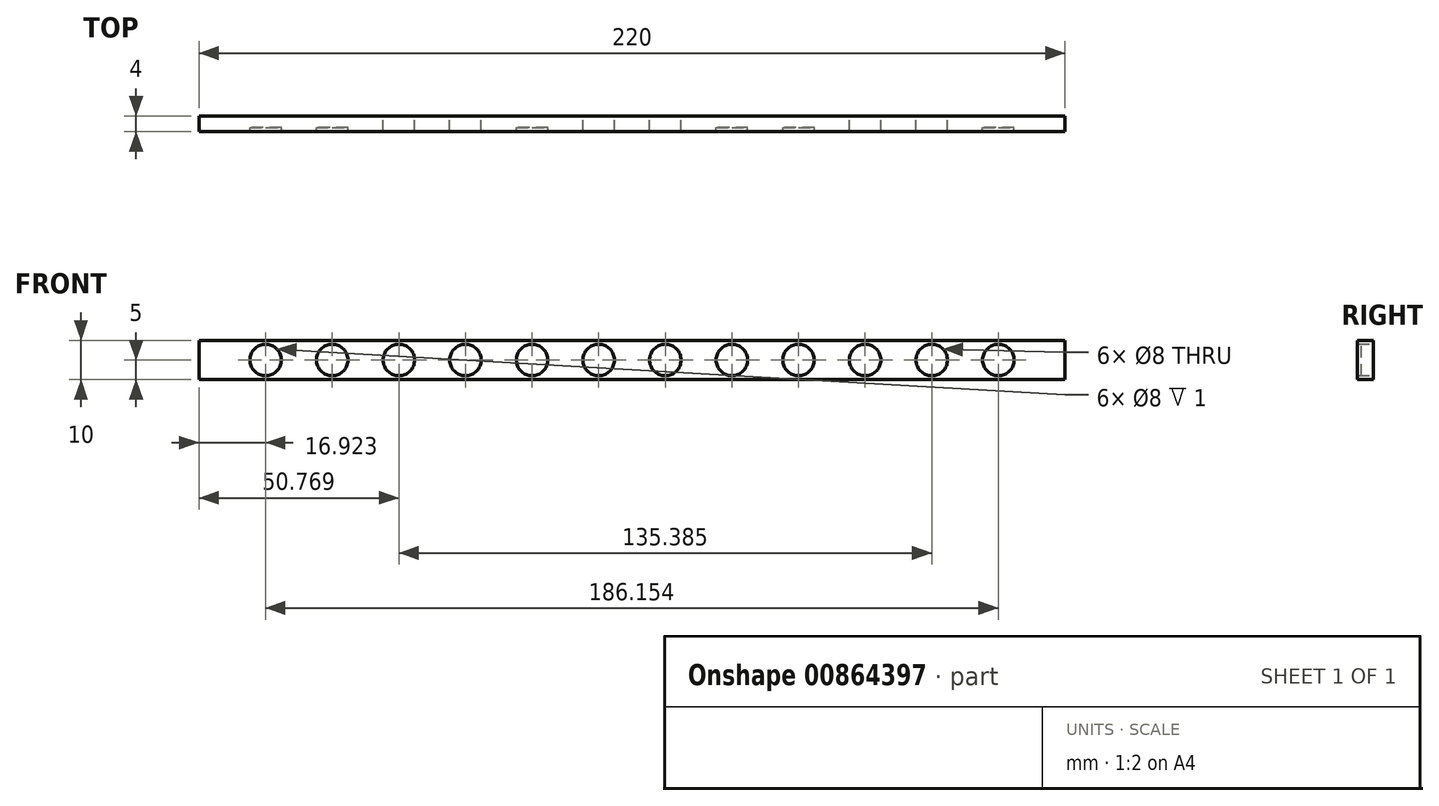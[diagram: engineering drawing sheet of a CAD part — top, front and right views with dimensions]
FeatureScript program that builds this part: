
annotation { "Feature Type Name" : "Feature", "Feature Type Description" : "" }
export const myFeature = defineFeature(function(context is Context, id is Id, definition is map)
    precondition{}
    {
        {
            var Q0;
            Q0=qCreatedBy(makeId("Front.planeOp"),FACE);
            var sketch = newSketch(context, id + "F0", { "sketchPlane" : qUnion([Q0])});
            skLineSegment(sketch, "E0", {"start": v(0, 0) * mm, "end": v(0, 10) * mm});
            skLineSegment(sketch, "E1", {"start": v(0, 10) * mm, "end": v(220, 10) * mm});
            skLineSegment(sketch, "E2", {"start": v(220, 10) * mm, "end": v(220, 0) * mm});
            skLineSegment(sketch, "E3", {"start": v(220, 0) * mm, "end": v(0, 0) * mm});
            skCircle(sketch, "E4", {"center": v(16.92, 5) * mm, "radius": 4 * mm});
            skCircle(sketch, "E5.MirrorC", {"center": v(50.77, 5) * mm, "radius": 4 * mm});
            skCircle(sketch, "E6.MirrorC", {"center": v(84.62, 5) * mm, "radius": 4 * mm});
            skCircle(sketch, "E7", {"center": v(33.85, 5) * mm, "radius": 4 * mm});
            skCircle(sketch, "E8.MirrorC", {"center": v(67.7, 5) * mm, "radius": 4 * mm});
            skCircle(sketch, "E9.MirrorC", {"center": v(118.46, 5) * mm, "radius": 4 * mm});
            skCircle(sketch, "E10.MirrorC", {"center": v(135.38, 5) * mm, "radius": 4 * mm});
            skCircle(sketch, "E11.MirrorC", {"center": v(169.23, 5) * mm, "radius": 4 * mm});
            skCircle(sketch, "E12.MirrorC", {"center": v(152.3, 5) * mm, "radius": 4 * mm});
            skCircle(sketch, "E13.MirrorC", {"center": v(186.15, 5) * mm, "radius": 4 * mm});
            skCircle(sketch, "E14.MirrorC", {"center": v(101.54, 5) * mm, "radius": 4 * mm});
            skCircle(sketch, "E15.MirrorC", {"center": v(203.08, 5) * mm, "radius": 4 * mm});
            skSolve(sketch);
        }
        {
            var Q0;
            Q0=makeQuery(id+"F0.imprint","IMPRINT",FACE,{"disambiguationData":[TD([[makeQuery(id+"F0.imprint","IMPRINT",EDGE,{"derivedFrom":sQuery(id+"F0.wireOp",EDGE,"E1")}),-1.0]])]});
            extrude(context, id + "F1", {"entities" : qUnion([Q0]), "depth" : 1 * mm, "offsetDistance" : 25 * mm});
        }
        {
            var Q0;
            Q0=makeQuery(id+"F0.imprint","IMPRINT",FACE,{"disambiguationData":[TD([[makeQuery(id+"F0.imprint","IMPRINT",EDGE,{"derivedFrom":sQuery(id+"F0.wireOp",EDGE,"E4")}),1.0]])]});
            var Q1;
            Q1=makeQuery(id+"F0.imprint","IMPRINT",FACE,{"disambiguationData":[TD([[makeQuery(id+"F0.imprint","IMPRINT",EDGE,{"derivedFrom":sQuery(id+"F0.wireOp",EDGE,"E7")}),1.0]])]});
            var Q2;
            Q2=makeQuery(id+"F0.imprint","IMPRINT",FACE,{"disambiguationData":[TD([[makeQuery(id+"F0.imprint","IMPRINT",EDGE,{"derivedFrom":sQuery(id+"F0.wireOp",EDGE,"E5.MirrorC")}),-1.0]])]});
            var Q3;
            Q3=makeQuery(id+"F0.imprint","IMPRINT",FACE,{"disambiguationData":[TD([[makeQuery(id+"F0.imprint","IMPRINT",EDGE,{"derivedFrom":sQuery(id+"F0.wireOp",EDGE,"E8.MirrorC")}),-1.0]])]});
            var Q4;
            Q4=makeQuery(id+"F0.imprint","IMPRINT",FACE,{"disambiguationData":[TD([[makeQuery(id+"F0.imprint","IMPRINT",EDGE,{"derivedFrom":sQuery(id+"F0.wireOp",EDGE,"E6.MirrorC")}),1.0]])]});
            var Q5;
            Q5=makeQuery(id+"F0.imprint","IMPRINT",FACE,{"disambiguationData":[TD([[makeQuery(id+"F0.imprint","IMPRINT",EDGE,{"derivedFrom":sQuery(id+"F0.wireOp",EDGE,"E14.MirrorC")}),-1.0]])]});
            var Q6;
            Q6=makeQuery(id+"F0.imprint","IMPRINT",FACE,{"disambiguationData":[TD([[makeQuery(id+"F0.imprint","IMPRINT",EDGE,{"derivedFrom":sQuery(id+"F0.wireOp",EDGE,"E10.MirrorC")}),1.0]])]});
            var Q7;
            Q7=makeQuery(id+"F0.imprint","IMPRINT",FACE,{"disambiguationData":[TD([[makeQuery(id+"F0.imprint","IMPRINT",EDGE,{"derivedFrom":sQuery(id+"F0.wireOp",EDGE,"E9.MirrorC")}),-1.0]])]});
            var Q8;
            Q8=makeQuery(id+"F0.imprint","IMPRINT",FACE,{"disambiguationData":[TD([[makeQuery(id+"F0.imprint","IMPRINT",EDGE,{"derivedFrom":sQuery(id+"F0.wireOp",EDGE,"E12.MirrorC")}),1.0]])]});
            var Q9;
            Q9=makeQuery(id+"F0.imprint","IMPRINT",FACE,{"disambiguationData":[TD([[makeQuery(id+"F0.imprint","IMPRINT",EDGE,{"derivedFrom":sQuery(id+"F0.wireOp",EDGE,"E15.MirrorC")}),1.0]])]});
            var Q10;
            Q10=makeQuery(id+"F0.imprint","IMPRINT",FACE,{"disambiguationData":[TD([[makeQuery(id+"F0.imprint","IMPRINT",EDGE,{"derivedFrom":sQuery(id+"F0.wireOp",EDGE,"E11.MirrorC")}),-1.0]])]});
            var Q11;
            Q11=makeQuery(id+"F0.imprint","IMPRINT",FACE,{"disambiguationData":[TD([[makeQuery(id+"F0.imprint","IMPRINT",EDGE,{"derivedFrom":sQuery(id+"F0.wireOp",EDGE,"E13.MirrorC")}),-1.0]])]});
            extrude(context, id + "F2", {"entities" : qUnion([Q0, Q1, Q2, Q3, Q4, Q5, Q6, Q7, Q8, Q9, Q10, Q11]), "operationType" : NewBodyOperationType.ADD, "oppositeDirection" : true, "depth" : 3 * mm, "offsetDistance" : 25 * mm});
        }
    });
